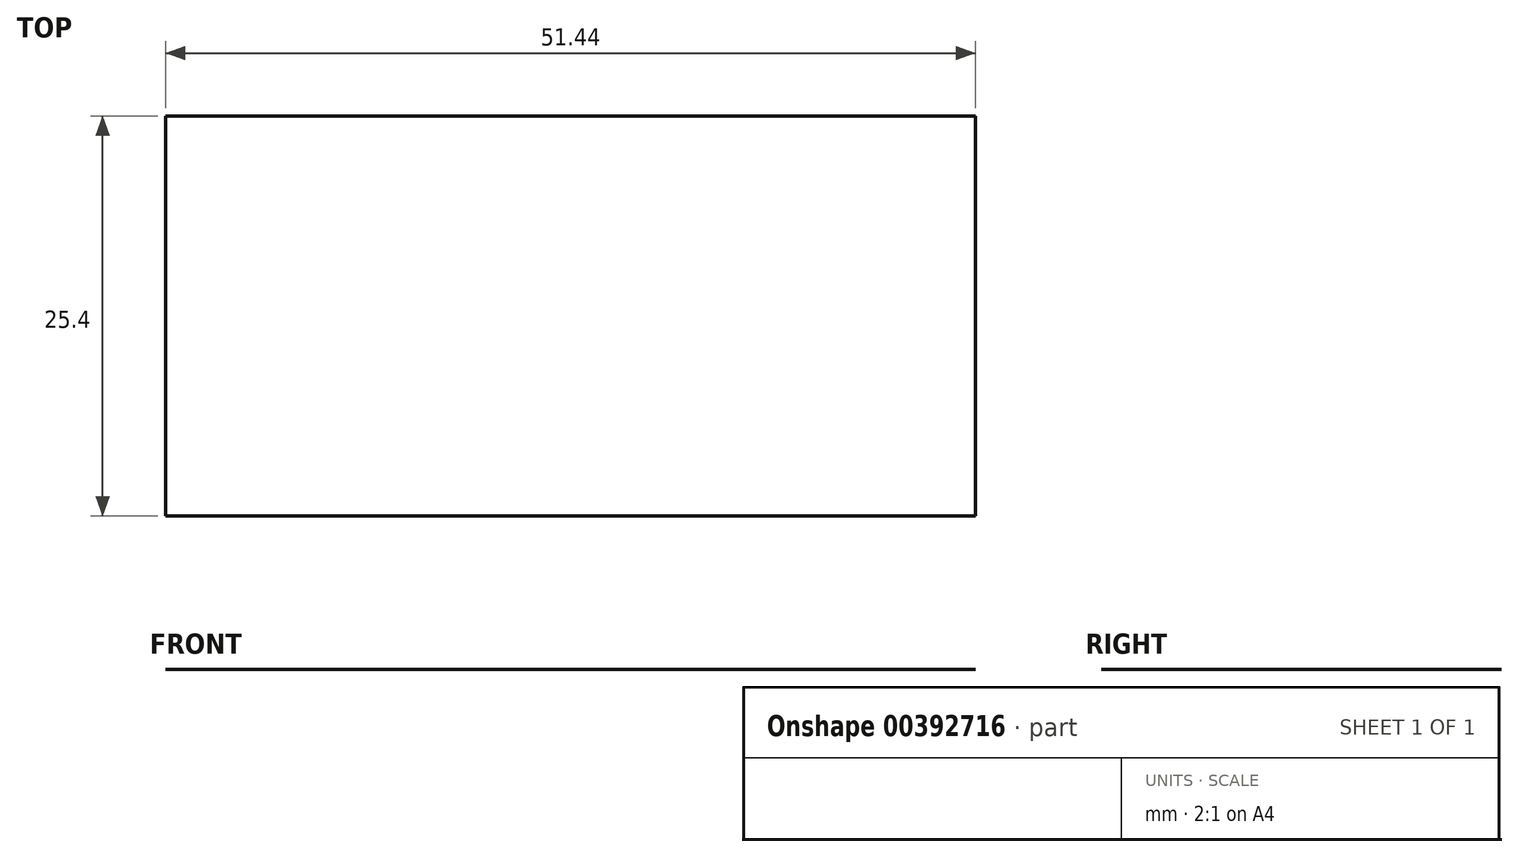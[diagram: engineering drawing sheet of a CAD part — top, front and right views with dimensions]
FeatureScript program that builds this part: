
annotation { "Feature Type Name" : "Feature", "Feature Type Description" : "" }
export const myFeature = defineFeature(function(context is Context, id is Id, definition is map)
    precondition{}
    {
        {
            var Q0;
            Q0=qCreatedBy(makeId("Front.planeOp"),FACE);
            var sketch = newSketch(context, id + "F0", { "sketchPlane" : qUnion([Q0])});
            skLineSegment(sketch, "E0.bottom", {"start": v(25.72, 17.2) * mm, "end": v(-25.72, 17.2) * mm});
            skLineSegment(sketch, "E0.top", {"start": v(25.72, -17.2) * mm, "end": v(-25.72, -17.2) * mm});
            skLineSegment(sketch, "E0.left", {"start": v(25.72, 17.2) * mm, "end": v(25.72, -17.2) * mm});
            skLineSegment(sketch, "E0.right", {"start": v(-25.72, 17.2) * mm, "end": v(-25.72, -17.2) * mm});
            skPoint(sketch, "E0.middle", {"position": v(0, 0) * mm});
            skSolve(sketch);
        }
        {
            var Q0;
            Q0=sQuery(id+"F0.wireOp",EDGE,"E0.bottom");
            extrude(context, id + "F1", {"bodyType" : ToolBodyType.SURFACE, "surfaceEntities" : qUnion([Q0]), "depth" : 25.4 * mm});
        }
    });
